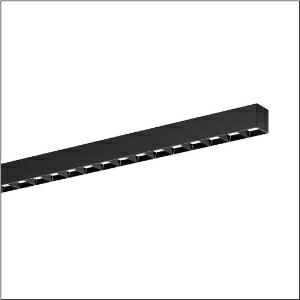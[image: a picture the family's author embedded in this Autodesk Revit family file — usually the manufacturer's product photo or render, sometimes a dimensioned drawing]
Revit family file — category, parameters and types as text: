
# Revit family: silica_r__21_51mx22tat4b_b010
name_source: partatom
category: Lighting Fixtures
units: mm (PartAtom-declared; Revit-internal decimal feet)

## family parameters
Cut with Voids When Loaded = No
Host = Face
Light Source = No
Part Type = Normal
Room Calculation Point = No
Round Connector Dimension = Use Diameter
Shared = No

## types (1)
- --- (1 x LED, 3720 lm, 32.1 W, 6500K)
    Apparent Load = 32 VA
    CIE Flux Codes = 84 100 100 100 100
    Color Rendering = 80
    Color Temperature = 6500K
    Default Elevation = 1800 mm
    Description = Silica® 21, office luminaire, primary light control with darklight reflector, of PMMA, black, CAT 2 (L<= 3000cd/m²), light emission: direct distribution, primary light characteristic: symmetric, installation type: surface-mounted, LED, rated luminous flux: 3.720lm, luminous efficacy: 110lm/W, light colour: 8tw, colour temperature: 2700..6500K, control gear: ECG DALI, with terminal, 3+2-pole, max. 2.5mm², mains connection: 220..240V, AC, 50/60Hz, rated input power: 33.8W, luminaire housing, of aluminium, jet black (RAL 9005), length: 1.204mm, width: 53mm, height: 53mm, protection rating (complete): IP20, insulation class (complete): insulation class I (protective earthing), certification: CE, permissible operating ambient temperature: 0..+35°C, standard: EN 50419, packaging unit: 1 piece
    Height = 0 mm  [stored 0 ft]
    Lamp = 1 x LED
    Lamp Light Flux = 3720 lm
    Lamp Power = 32.1 W
    Lamp count = 1
    Length = 1204 mm
    Luminous efficacy = 116 lm/W
    Manufacturer = Siteco
    ModVariant = No
    Model = 51MX22TAT4B
    Mounting Place = Ceiling
    Mounting Type = Recessed
    Number of Poles = 1
    OnlyDefault = Yes
    Power Factor = 1
    Product Name = Silica® 21
    Product group = office luminaire | ceiling recessed
    ProductGroupID = 401
    Protection Class = Protection class I
    Protection Degree = IP 20
    RLX_Detail_Level = 1
    RLX_Emergency_Light_Flux = 0 lm
    RLX_Emergency_Type = 0
    RLX_Emergency_Type_DB = No
    RlxData = <blob elided: 40325 chars, md5=52adeff8>
    Socket = socket
    Standby Power = 0 W
    System Light Flux = 3720 lm
    System Power = 32 W
    Type Comments = individual setting
    Type Image = l_1297756.jpg
    URL = http://relux.com
    VarID = @adj_071467
    Voltage = 0 V
    Weight = 0.00 kg
    Width = 53 mm

note: [stored X ft] marks values corroborated as IEEE doubles in the binary element streams (Revit-internal decimal feet)

## geometry (parser evidence)
native form markers: Blend x4, Sweep x10
no freeform markers — native parametric forms only
